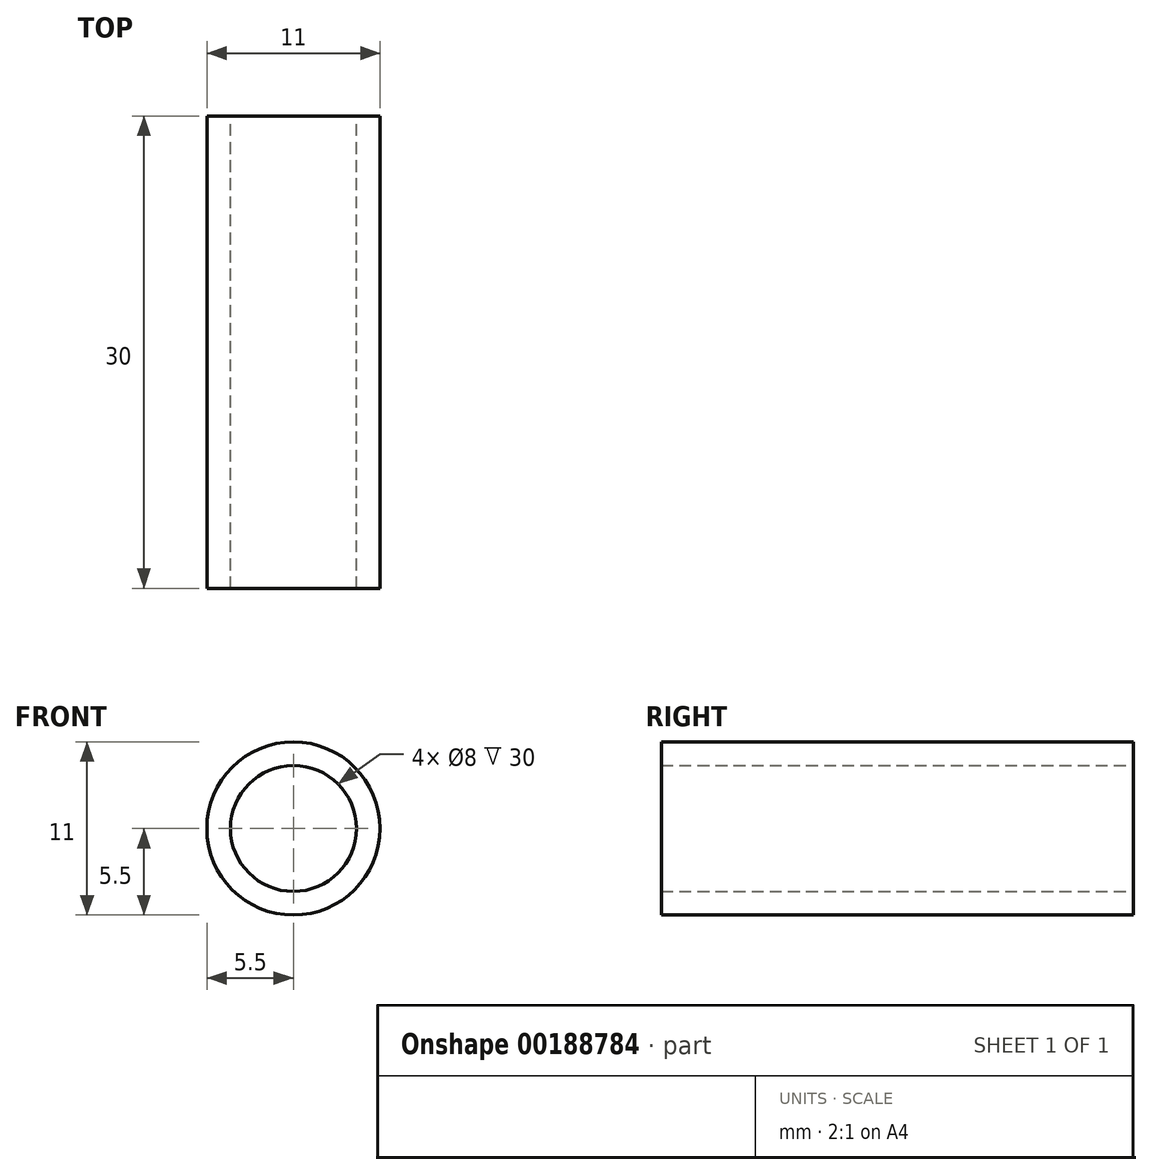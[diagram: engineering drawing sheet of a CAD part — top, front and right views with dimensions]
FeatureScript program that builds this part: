
annotation { "Feature Type Name" : "Feature", "Feature Type Description" : "" }
export const myFeature = defineFeature(function(context is Context, id is Id, definition is map)
    precondition{}
    {
        {
            var Q0;
            Q0=qCreatedBy(makeId("Front.planeOp"),FACE);
            var sketch = newSketch(context, id + "F0", { "sketchPlane" : qUnion([Q0])});
            skCircle(sketch, "E0", {"center": v(0, 0) * mm, "radius": 4 * mm});
            skCircle(sketch, "E1", {"center": v(0, 0) * mm, "radius": 5.5 * mm});
            skSolve(sketch);
        }
        {
            var Q0;
            Q0=makeQuery(id+"F0.imprint","IMPRINT",FACE,{"disambiguationData":[TD([[makeQuery(id+"F0.imprint","IMPRINT",EDGE,{"derivedFrom":sQuery(id+"F0.wireOp",EDGE,"E0")}),-1.0]])]});
            extrude(context, id + "F1", {"entities" : qUnion([Q0]), "depth" : 30 * mm});
        }
    });
